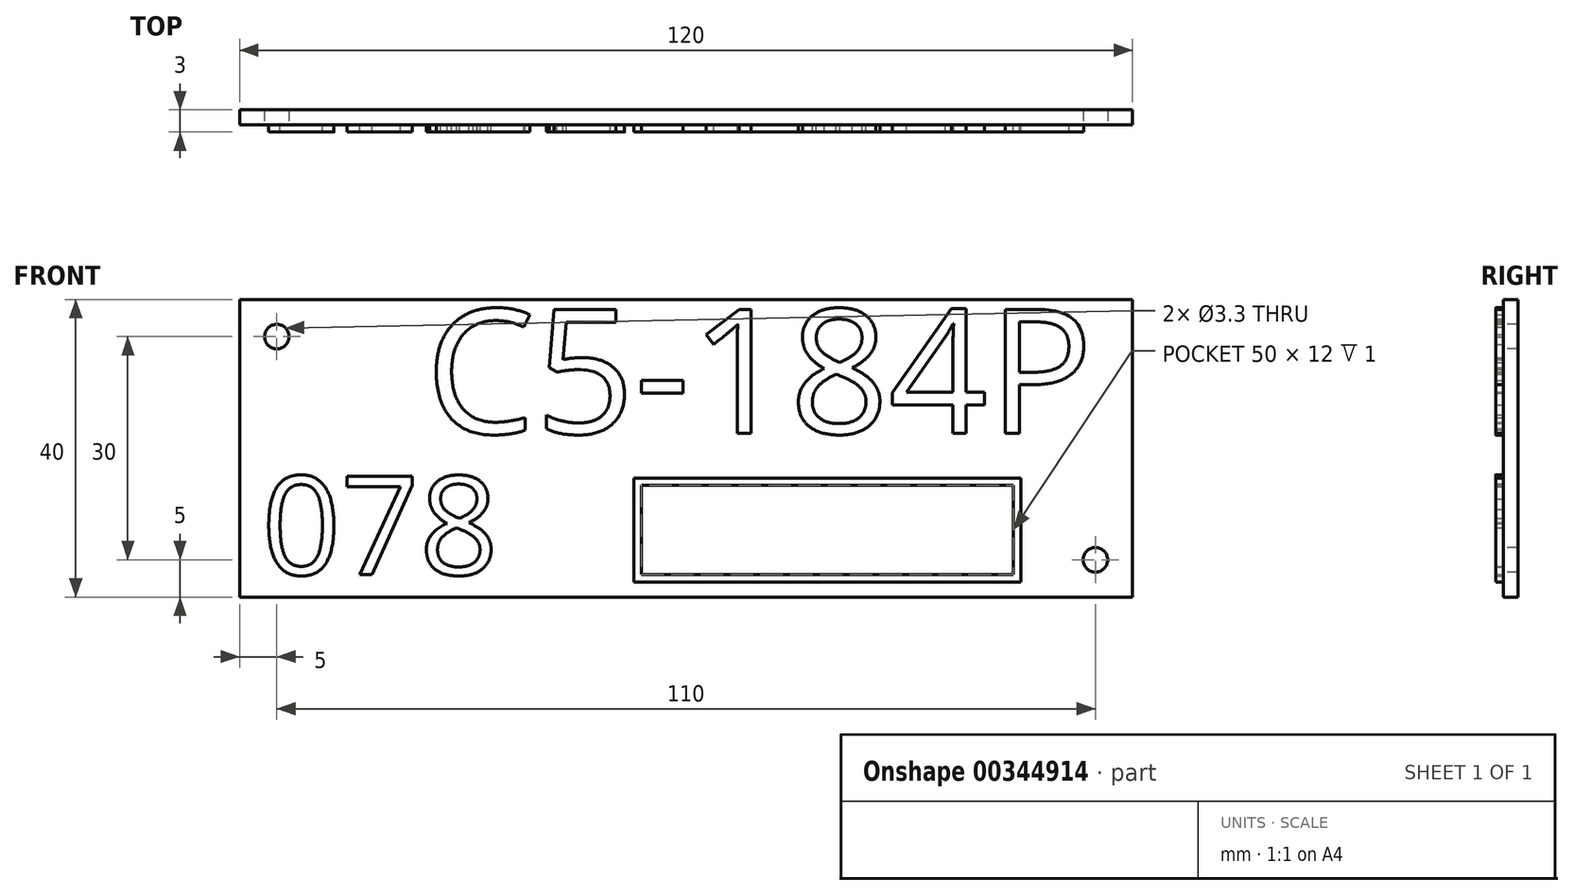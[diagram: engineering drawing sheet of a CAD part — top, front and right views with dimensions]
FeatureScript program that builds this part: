
annotation { "Feature Type Name" : "Feature", "Feature Type Description" : "" }
export const myFeature = defineFeature(function(context is Context, id is Id, definition is map)
    precondition{}
    {
        {
            var Q0;
            Q0=qCreatedBy(makeId("Front.planeOp"),FACE);
            var sketch = newSketch(context, id + "F0", { "sketchPlane" : qUnion([Q0])});
            skLineSegment(sketch, "E0.bottom", {"start": v(60, -20) * mm, "end": v(-60, -20) * mm});
            skLineSegment(sketch, "E0.top", {"start": v(60, 20) * mm, "end": v(-60, 20) * mm});
            skLineSegment(sketch, "E0.left", {"start": v(60, -20) * mm, "end": v(60, 20) * mm});
            skLineSegment(sketch, "E0.right", {"start": v(-60, -20) * mm, "end": v(-60, 20) * mm});
            skPoint(sketch, "E0.middle", {"position": v(0, 0) * mm});
            skSolve(sketch);
        }
        {
            var Q0;
            Q0=makeQuery(id+"F0.imprint","IMPRINT",FACE,{"disambiguationData":[TD([[makeQuery(id+"F0.imprint","IMPRINT",EDGE,{"derivedFrom":sQuery(id+"F0.wireOp",EDGE,"E0.bottom")}),-1.0]])]});
            extrude(context, id + "F1", {"entities" : qUnion([Q0]), "depth" : 2 * mm});
        }
        {
            var Q0;
            Q0=makeQuery(id+"F1.opExtrude","CAP_FACE",FACE,{"disambiguationData":[OSD([sQuery(id+"F0.wireOp",EDGE,"E0.bottom"),sQuery(id+"F0.wireOp",EDGE,"E0.top"),sQuery(id+"F0.wireOp",EDGE,"E0.left"),sQuery(id+"F0.wireOp",EDGE,"E0.right")])],"isStart":false});
            var sketch = newSketch(context, id + "F2", { "sketchPlane" : qUnion([Q0])});
            skPoint(sketch, "E1", {"position": v(-55, 15) * mm});
            skPoint(sketch, "E2", {"position": v(55, -15) * mm});
            skSolve(sketch);
        }
        {
            var Q0;
            Q0=sQuery(id+"F2.wireOp",VERTEX,"E1");
            var Q1;
            Q1=sQuery(id+"F2.wireOp",VERTEX,"E2");
            var Q2;
            Q2=makeQuery(id+"F1.opExtrude","SWEPT_BODY",BODY,{"disambiguationData":[OSD([sQuery(id+"F0.wireOp",EDGE,"E0.bottom"),sQuery(id+"F0.wireOp",EDGE,"E0.top"),sQuery(id+"F0.wireOp",EDGE,"E0.left"),sQuery(id+"F0.wireOp",EDGE,"E0.right")])]});
            hole(context, id + "F3", {"style" : HoleStyle.SIMPLE, "endStyle" : HoleEndStyle.THROUGH, "holeDiameter" : 3.3 * mm, "locations" : qUnion([Q0, Q1]), "scope" : qUnion([Q2]), "isTappedThrough" : true});
        }
        {
            var Q0;
            Q0=makeQuery(id+"F1.opExtrude","CAP_FACE",FACE,{"disambiguationData":[OSD([sQuery(id+"F0.wireOp",EDGE,"E0.bottom"),sQuery(id+"F0.wireOp",EDGE,"E0.top"),sQuery(id+"F0.wireOp",EDGE,"E0.left"),sQuery(id+"F0.wireOp",EDGE,"E0.right")])],"isStart":false});
            var sketch = newSketch(context, id + "F4", { "sketchPlane" : qUnion([Q0])});
            skText(sketch, "E3", { "text": "C5-184P", "fontName": "OpenSans-Regular.ttf"});
            const initialGuessF4  = {"E3": [-0.035, 0.002, 1, 0, 0.0168]};
            skSetInitialGuess(sketch, initialGuessF4);
            skSolve(sketch);
        }
        {
            var Q0;
            Q0=qSketchRegion(id+"F4",true);
            extrude(context, id + "F5", {"entities" : qUnion([Q0]), "operationType" : NewBodyOperationType.ADD, "depth" : 1 * mm});
        }
        {
            var Q0;
            {var subQ0=sQuery(id+"F0.wireOp",EDGE,"E0.top");var subQ1=sQuery(id+"F0.wireOp",EDGE,"E0.left");var subQ2=sQuery(id+"F0.wireOp",EDGE,"E0.right");var subQ3=sQuery(id+"F0.wireOp",EDGE,"E0.bottom");Q0=makeQuery(id+"F5.boolean.opBoolean","SPLIT",FACE,{"disambiguationData":[TD([makeQuery(id+"F1.opExtrude","SWEPT_FACE",FACE,{"disambiguationData":[OSD([subQ3])]})])],"derivedFrom":makeQuery(id+"F1.opExtrude","CAP_FACE",FACE,{"disambiguationData":[OSD([subQ3,subQ0,subQ1,subQ2])],"isStart":false})});}
            var sketch = newSketch(context, id + "F6", { "sketchPlane" : qUnion([Q0])});
            skText(sketch, "E4", { "text": "078", "fontName": "OpenSans-Regular.ttf"});
            const initialGuessF6  = {"E4": [-0.057, -0.017, 1, 0, 0.01333]};
            skSetInitialGuess(sketch, initialGuessF6);
            skSolve(sketch);
        }
        {
            var Q0;
            Q0=qSketchRegion(id+"F6",true);
            extrude(context, id + "F7", {"entities" : qUnion([Q0]), "operationType" : NewBodyOperationType.ADD, "depth" : 1 * mm});
        }
        {
            var Q0;
            {var subQ46=sQuery(id+"F0.wireOp",EDGE,"E0.top");var subQ48=sQuery(id+"F0.wireOp",EDGE,"E0.left");var subQ66=sQuery(id+"F0.wireOp",EDGE,"E0.right");var subQ76=sQuery(id+"F0.wireOp",EDGE,"E0.bottom");var subQ77=makeQuery(id+"F1.opExtrude","SWEPT_FACE",FACE,{"disambiguationData":[OSD([subQ76])]});Q0=makeQuery(id+"F7.boolean.opBoolean","SPLIT",FACE,{"disambiguationData":[TD([subQ77])],"derivedFrom":makeQuery(id+"F5.boolean.opBoolean","SPLIT",FACE,{"disambiguationData":[TD([subQ77])],"derivedFrom":makeQuery(id+"F1.opExtrude","CAP_FACE",FACE,{"disambiguationData":[OSD([subQ76,subQ46,subQ48,subQ66])],"isStart":false})})});}
            var sketch = newSketch(context, id + "F8", { "sketchPlane" : qUnion([Q0])});
            skLineSegment(sketch, "E5.bottom", {"start": v(45, -18) * mm, "end": v(-7, -18) * mm});
            skLineSegment(sketch, "E5.top", {"start": v(45, -4) * mm, "end": v(-7, -4) * mm});
            skLineSegment(sketch, "E5.left", {"start": v(45, -18) * mm, "end": v(45, -4) * mm});
            skLineSegment(sketch, "E5.right", {"start": v(-7, -18) * mm, "end": v(-7, -4) * mm});
            skPoint(sketch, "E5.middle", {"position": v(19, -11) * mm});
            skLineSegment(sketch, "E6.0", {"start": v(44, -5) * mm, "end": v(-6, -5) * mm});
            skLineSegment(sketch, "E6.1", {"start": v(44, -17) * mm, "end": v(44, -5) * mm});
            skLineSegment(sketch, "E6.2", {"start": v(44, -17) * mm, "end": v(-6, -17) * mm});
            skLineSegment(sketch, "E6.3", {"start": v(-6, -17) * mm, "end": v(-6, -5) * mm});
            skSolve(sketch);
        }
        {
            var Q0;
            Q0=makeQuery(id+"F8.imprint","IMPRINT",FACE,{"disambiguationData":[TD([[makeQuery(id+"F8.imprint","IMPRINT",EDGE,{"derivedFrom":sQuery(id+"F8.wireOp",EDGE,"E5.bottom")}),-1.0]])]});
            extrude(context, id + "F9", {"entities" : qUnion([Q0]), "operationType" : NewBodyOperationType.ADD, "depth" : 1 * mm});
        }
    });
